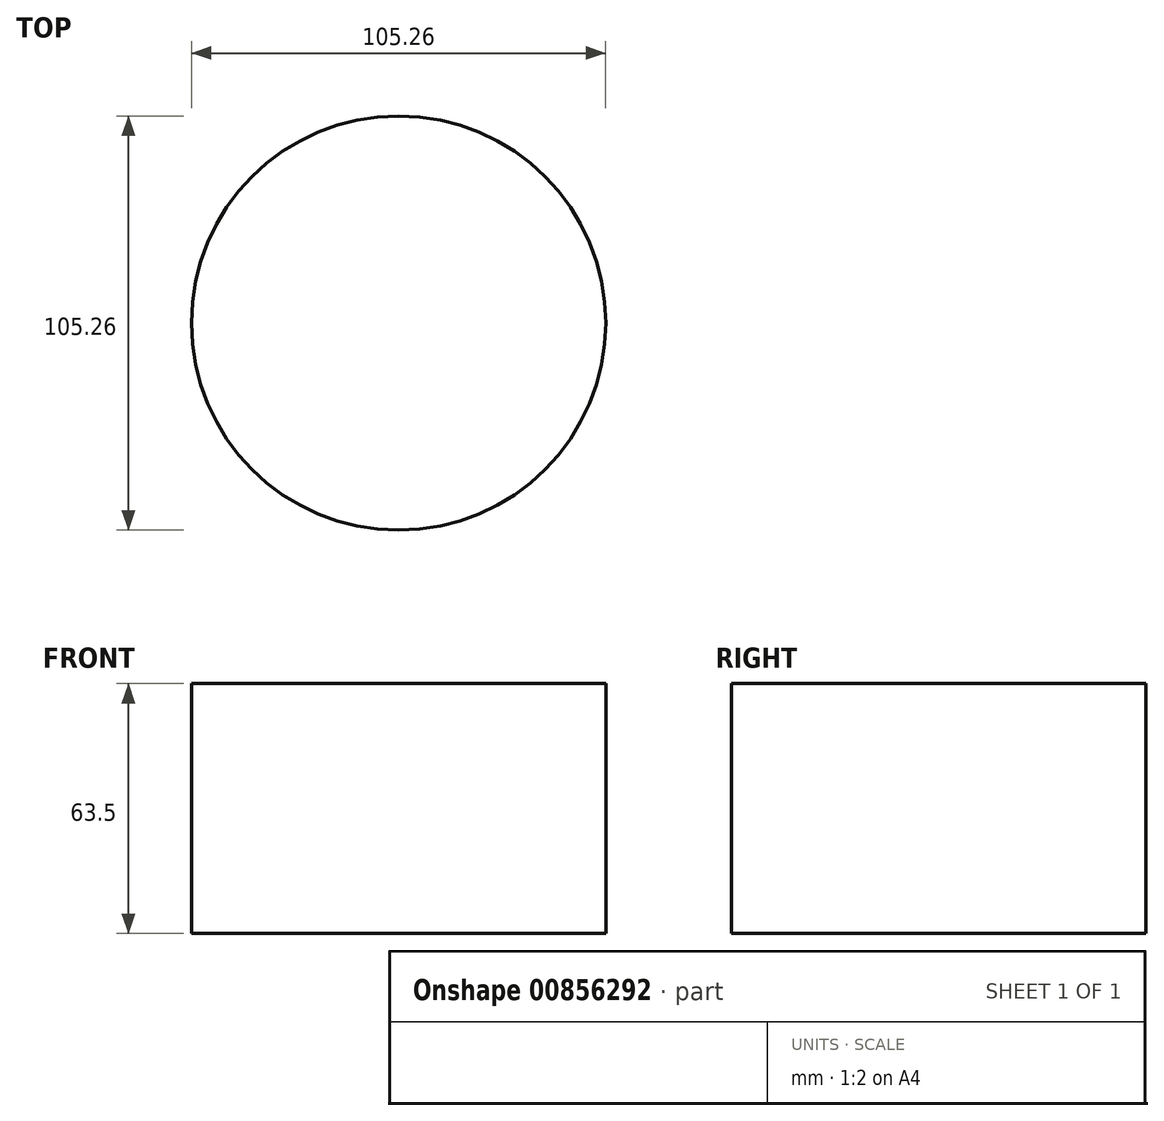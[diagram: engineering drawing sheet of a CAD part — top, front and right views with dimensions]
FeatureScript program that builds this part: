
annotation { "Feature Type Name" : "Feature", "Feature Type Description" : "" }
export const myFeature = defineFeature(function(context is Context, id is Id, definition is map)
    precondition{}
    {
        {
            var Q0;
            Q0=qCreatedBy(makeId("Top.planeOp"),FACE);
            var sketch = newSketch(context, id + "F0", { "sketchPlane" : qUnion([Q0])});
            skCircle(sketch, "E0", {"center": v(0, 0) * mm, "radius": 52.63 * mm});
            skSolve(sketch);
        }
        {
            var Q0;
            Q0=makeQuery(id+"F0.imprint","IMPRINT",FACE,{"disambiguationData":[TD([[makeQuery(id+"F0.imprint","IMPRINT",EDGE,{"derivedFrom":sQuery(id+"F0.wireOp",EDGE,"E0")}),1.0]])]});
            extrude(context, id + "F1", {"entities" : qUnion([Q0]), "depth" : 63.5 * mm, "offsetDistance" : 25 * mm});
        }
    });
